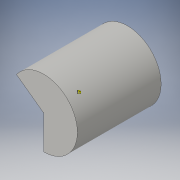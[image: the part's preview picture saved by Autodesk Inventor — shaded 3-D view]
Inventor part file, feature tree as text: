
AUTODESK INVENTOR PART (.ipt)
format: ipt  version: 2016 (Build 200138000, 138)  size: 100,352 bytes
history: native  units: in
note: dims shown in document units (in); Inventor stores cm internally (conversion verified against a paired STEP export)
features: revolve x1, sketch x1
ambient origin geometry x8: Origin, YZ Plane, XZ Plane, XY Plane, X Axis, Y Axis, Z Axis, Center Point
bodies: Solid1 (feature_tree)
feature tree (2):
  revolve  "Revolution1"  [1 undecoded]
  sketch  "Sketch1"  dims[d0=1.6079in]
note: 1 required parameter value undecoded (feature->parameter linkage not recoverable at this tier; creation-order binding heuristic only, values carry confidence <= 0.55)
